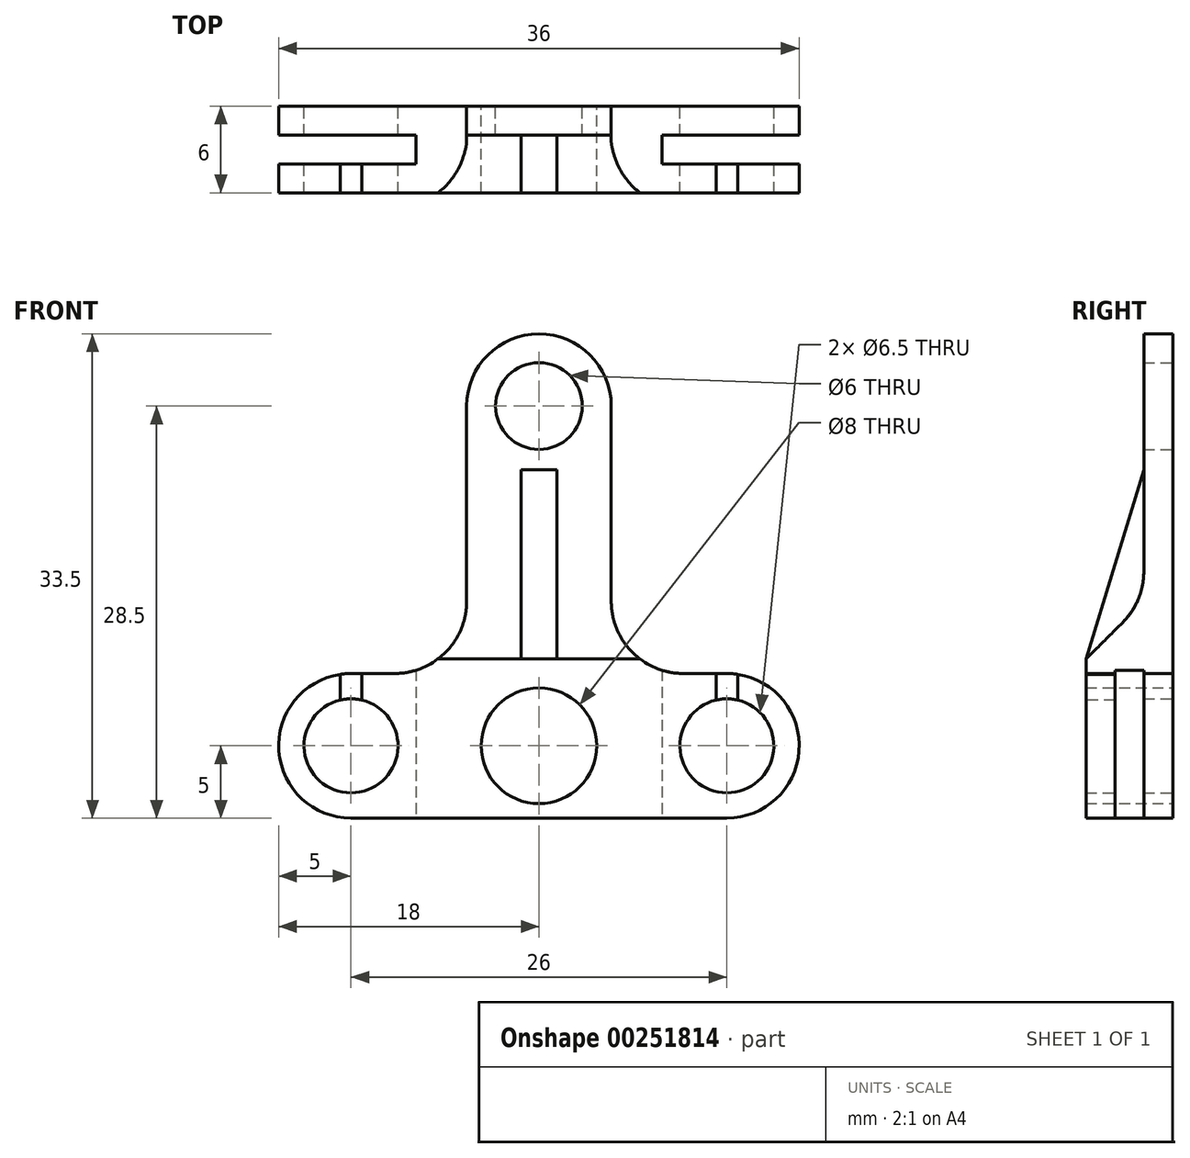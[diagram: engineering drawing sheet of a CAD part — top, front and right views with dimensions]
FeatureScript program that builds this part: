
annotation { "Feature Type Name" : "Feature", "Feature Type Description" : "" }
export const myFeature = defineFeature(function(context is Context, id is Id, definition is map)
    precondition{}
    {
        {
            var Q0;
            Q0=qCreatedBy(makeId("Front.planeOp"),FACE);
            var sketch = newSketch(context, id + "F0", { "sketchPlane" : qUnion([Q0])});
            skCircle(sketch, "E0", {"center": v(0, 0) * mm, "radius": 4 * mm});
            skLineSegment(sketch, "E1", {"start": v(-41, 0) * mm, "end": v(51.04, 0) * mm, "construction": true});
            skLineSegment(sketch, "E2", {"start": v(0, -26.28) * mm, "end": v(0, 53.97) * mm, "construction": true});
            skCircle(sketch, "E3", {"center": v(-13, 0) * mm, "radius": 3.25 * mm});
            skCircle(sketch, "E4", {"center": v(13, 0) * mm, "radius": 3.25 * mm});
            skLineSegment(sketch, "E5", {"start": v(-13, -5) * mm, "end": v(13, -5) * mm});
            skLineSegment(sketch, "E6", {"start": v(-13, 5) * mm, "end": v(-12.25, 5) * mm});
            skLineSegment(sketch, "E7", {"start": v(-13, -8.91) * mm, "end": v(-13, 11.18) * mm, "construction": true});
            skLineSegment(sketch, "E8", {"start": v(13, -9.6) * mm, "end": v(13, 11.08) * mm, "construction": true});
            skArc(sketch, "E9", {"start": v(-13, 5) * mm, "mid": v(-18, 0) * mm, "end": v(-13, -5) * mm});
            skArc(sketch, "E10", {"start": v(13, -5) * mm, "mid": v(18, 0) * mm, "end": v(13, 5) * mm});
            skLineSegment(sketch, "E11.left", {"start": v(-13.75, 4.94) * mm, "end": v(-13.75, 3.16) * mm});
            skLineSegment(sketch, "E11.right", {"start": v(-12.25, 5) * mm, "end": v(-12.25, 3.16) * mm});
            skLineSegment(sketch, "E12.MirrorCS", {"start": v(12.25, 5) * mm, "end": v(12.25, 3.16) * mm});
            skLineSegment(sketch, "E13.MirrorCS", {"start": v(13.75, 4.94) * mm, "end": v(13.75, 3.16) * mm});
            skCircle(sketch, "E14", {"center": v(0, 23.5) * mm, "radius": 3 * mm});
            skLineSegment(sketch, "E15", {"start": v(-10.87, 23.5) * mm, "end": v(15.23, 23.5) * mm, "construction": true});
            skLineSegment(sketch, "E16.trimOffspring", {"start": v(12.25, 5) * mm, "end": v(13, 5) * mm});
            skLineSegment(sketch, "E17", {"start": v(-5, 23.5) * mm, "end": v(-5, 10) * mm});
            skLineSegment(sketch, "E18", {"start": v(5, 23.5) * mm, "end": v(5, 10) * mm});
            skArc(sketch, "E19", {"start": v(5, 23.5) * mm, "mid": v(0, 28.5) * mm, "end": v(-5, 23.5) * mm});
            skArc(sketch, "E20", {"start": v(5, 10) * mm, "mid": v(6.46, 6.46) * mm, "end": v(10, 5) * mm});
            skLineSegment(sketch, "E21", {"start": v(12.25, 5) * mm, "end": v(10, 5) * mm});
            skArc(sketch, "E22.MirrorCS", {"start": v(-5, 10) * mm, "mid": v(-6.46, 6.46) * mm, "end": v(-10, 5) * mm});
            skLineSegment(sketch, "E23.MirrorCS", {"start": v(-12.25, 5) * mm, "end": v(-10, 5) * mm});
            skLineSegment(sketch, "E24", {"start": v(-7, 6) * mm, "end": v(7, 6) * mm});
            skLineSegment(sketch, "E25.bottom", {"start": v(-1.25, 6) * mm, "end": v(1.25, 6) * mm});
            skLineSegment(sketch, "E25.top", {"start": v(-1.25, 19) * mm, "end": v(1.25, 19) * mm});
            skLineSegment(sketch, "E25.left", {"start": v(-1.25, 6) * mm, "end": v(-1.25, 19) * mm});
            skLineSegment(sketch, "E25.right", {"start": v(1.25, 6) * mm, "end": v(1.25, 19) * mm});
            skSolve(sketch);
        }
        {
            var Q0;
            Q0 = qSketchRegion(id + "F0", true);
            extrude(context, id + "F1", {"entities" : qUnion([Q0]), "depth" : 6 * mm});
        }
        {
            var Q0;
            Q0=qCreatedBy(makeId("Right.planeOp"),FACE);
            var sketch = newSketch(context, id + "F2", { "sketchPlane" : qUnion([Q0])});
            skPoint(sketch, "E26.0", {"position": v(-6, 6) * mm});
            skPoint(sketch, "E27.0", {"position": v(-6, 28.5) * mm});
            skLineSegment(sketch, "E28", {"start": v(-2, 28.5) * mm, "end": v(-2, 12.07) * mm});
            skLineSegment(sketch, "E29", {"start": v(-2, 28.5) * mm, "end": v(-6, 28.5) * mm});
            skLineSegment(sketch, "E30", {"start": v(-6, 28.5) * mm, "end": v(-6, 6) * mm});
            skLineSegment(sketch, "E31", {"start": v(-6, 6) * mm, "end": v(-3.46, 8.54) * mm});
            skArc(sketch, "E32", {"start": v(-2, 12.07) * mm, "mid": v(-2.38, 10.16) * mm, "end": v(-3.46, 8.54) * mm});
            skLineSegment(sketch, "E33", {"start": v(-6, 6) * mm, "end": v(-2, 19.08) * mm});
            skSolve(sketch);
        }
        {
            var Q0;
            Q0 = qSketchRegion(id + "F2", true);
            extrude(context, id + "F3", {"entities" : qUnion([Q0]), "operationType" : NewBodyOperationType.REMOVE, "endBound" : BoundingType.SYMMETRIC, "oppositeDirection" : true, "depth" : 25 * mm});
        }
        {
            var Q0;
            Q0=qCreatedBy(makeId("Right.planeOp"),FACE);
            var sketch = newSketch(context, id + "F4", { "sketchPlane" : qUnion([Q0])});
            skLineSegment(sketch, "E34.0", {"start": v(-6, 6) * mm, "end": v(-2, 19.08) * mm});
            skLineSegment(sketch, "E35", {"start": v(0, 19.08) * mm, "end": v(0, 6) * mm});
            skLineSegment(sketch, "E36", {"start": v(-6, 6) * mm, "end": v(0, 6) * mm});
            skLineSegment(sketch, "E37", {"start": v(-2, 19.08) * mm, "end": v(0, 19.08) * mm});
            skSolve(sketch);
        }
        {
            var Q0;
            Q0 = qSketchRegion(id + "F4", true);
            extrude(context, id + "F5", {"entities" : qUnion([Q0]), "operationType" : NewBodyOperationType.ADD, "endBound" : BoundingType.SYMMETRIC, "depth" : 2.5 * mm});
        }
        {
            var Q0;
            Q0=makeQuery(id+"F1.opExtrude","SWEPT_FACE",FACE,{"disambiguationData":[OSD([sQuery(id+"F0.wireOp",EDGE,"E5")])]});
            var sketch = newSketch(context, id + "F6", { "sketchPlane" : qUnion([Q0])});
            skPoint(sketch, "E38.0", {"position": v(-18, 6) * mm});
            skLineSegment(sketch, "E39", {"start": v(-18, 0) * mm, "end": v(-18, 6) * mm});
            skPoint(sketch, "E40.0", {"position": v(-18, 0) * mm});
            skLineSegment(sketch, "E41.bottom", {"start": v(-18, 2) * mm, "end": v(-8.5, 2) * mm});
            skLineSegment(sketch, "E41.top", {"start": v(-18, 4) * mm, "end": v(-8.5, 4) * mm});
            skLineSegment(sketch, "E41.left", {"start": v(-18, 2) * mm, "end": v(-18, 4) * mm});
            skLineSegment(sketch, "E41.right", {"start": v(-8.5, 2) * mm, "end": v(-8.5, 4) * mm});
            skLineSegment(sketch, "E42.MirrorCS", {"start": v(18, 2) * mm, "end": v(8.5, 2) * mm});
            skLineSegment(sketch, "E43.MirrorCS", {"start": v(18, 4) * mm, "end": v(8.5, 4) * mm});
            skLineSegment(sketch, "E44.MirrorCS", {"start": v(18, 2) * mm, "end": v(18, 4) * mm});
            skLineSegment(sketch, "E45.MirrorCS", {"start": v(8.5, 2) * mm, "end": v(8.5, 4) * mm});
            skSolve(sketch);
        }
        {
            var Q0;
            Q0 = qSketchRegion(id + "F6", true);
            extrude(context, id + "F7", {"entities" : qUnion([Q0]), "operationType" : NewBodyOperationType.REMOVE, "oppositeDirection" : true, "depth" : 25 * mm});
        }
        {
            var Q0;
            Q0=makeQuery(id+"F1.opExtrude","CAP_FACE",FACE,{"disambiguationData":[OSD([sQuery(id+"F0.wireOp",EDGE,"E0"),sQuery(id+"F0.wireOp",EDGE,"E3"),sQuery(id+"F0.wireOp",EDGE,"E4"),sQuery(id+"F0.wireOp",EDGE,"E5"),sQuery(id+"F0.wireOp",EDGE,"E6"),sQuery(id+"F0.wireOp",EDGE,"E9"),sQuery(id+"F0.wireOp",EDGE,"E10"),sQuery(id+"F0.wireOp",EDGE,"E14"),sQuery(id+"F0.wireOp",EDGE,"E16.trimOffspring"),sQuery(id+"F0.wireOp",EDGE,"E17"),sQuery(id+"F0.wireOp",EDGE,"E18"),sQuery(id+"F0.wireOp",EDGE,"E19"),sQuery(id+"F0.wireOp",EDGE,"E20"),sQuery(id+"F0.wireOp",EDGE,"E21"),sQuery(id+"F0.wireOp",EDGE,"E22.MirrorCS"),sQuery(id+"F0.wireOp",EDGE,"E23.MirrorCS"),sQuery(id+"F0.wireOp",EDGE,"E25.bottom"),sQuery(id+"F0.wireOp",EDGE,"E25.top"),sQuery(id+"F0.wireOp",EDGE,"E25.left"),sQuery(id+"F0.wireOp",EDGE,"E25.right")])],"isStart":false});
            var sketch = newSketch(context, id + "F8", { "sketchPlane" : qUnion([Q0])});
            skLineSegment(sketch, "E46.0", {"start": v(-12.25, 5) * mm, "end": v(-12.25, 3.16) * mm});
            skLineSegment(sketch, "E47.0", {"start": v(-13.75, 4.94) * mm, "end": v(-13.75, 3.16) * mm});
            skArc(sketch, "E48.0", {"start": v(-12.25, 3.16) * mm, "mid": v(-13, 3.25) * mm, "end": v(-13.75, 3.16) * mm});
            skArc(sketch, "E49.0", {"start": v(-13, 5) * mm, "mid": v(-13.38, 4.99) * mm, "end": v(-13.75, 4.94) * mm});
            skLineSegment(sketch, "E50.0", {"start": v(-13, 5) * mm, "end": v(-12.25, 5) * mm});
            skPoint(sketch, "E51.orphan", {"position": v(-13, -5) * mm});
            skLineSegment(sketch, "E52.MirrorCS", {"start": v(12.25, 5) * mm, "end": v(12.25, 3.16) * mm});
            skLineSegment(sketch, "E53.MirrorCS", {"start": v(13.75, 4.94) * mm, "end": v(13.75, 3.16) * mm});
            skArc(sketch, "E54.MirrorCS", {"start": v(12.25, 3.16) * mm, "mid": v(13, 3.25) * mm, "end": v(13.75, 3.16) * mm});
            skLineSegment(sketch, "E55.MirrorCS", {"start": v(13, 5) * mm, "end": v(12.25, 5) * mm});
            skArc(sketch, "E56.MirrorCS", {"start": v(13, 5) * mm, "mid": v(13.38, 4.99) * mm, "end": v(13.75, 4.94) * mm});
            skSolve(sketch);
        }
        {
            var Q0;
            Q0 = qSketchRegion(id + "F8", true);
            extrude(context, id + "F9", {"entities" : qUnion([Q0]), "operationType" : NewBodyOperationType.REMOVE, "oppositeDirection" : true, "depth" : 3 * mm});
        }
    });
